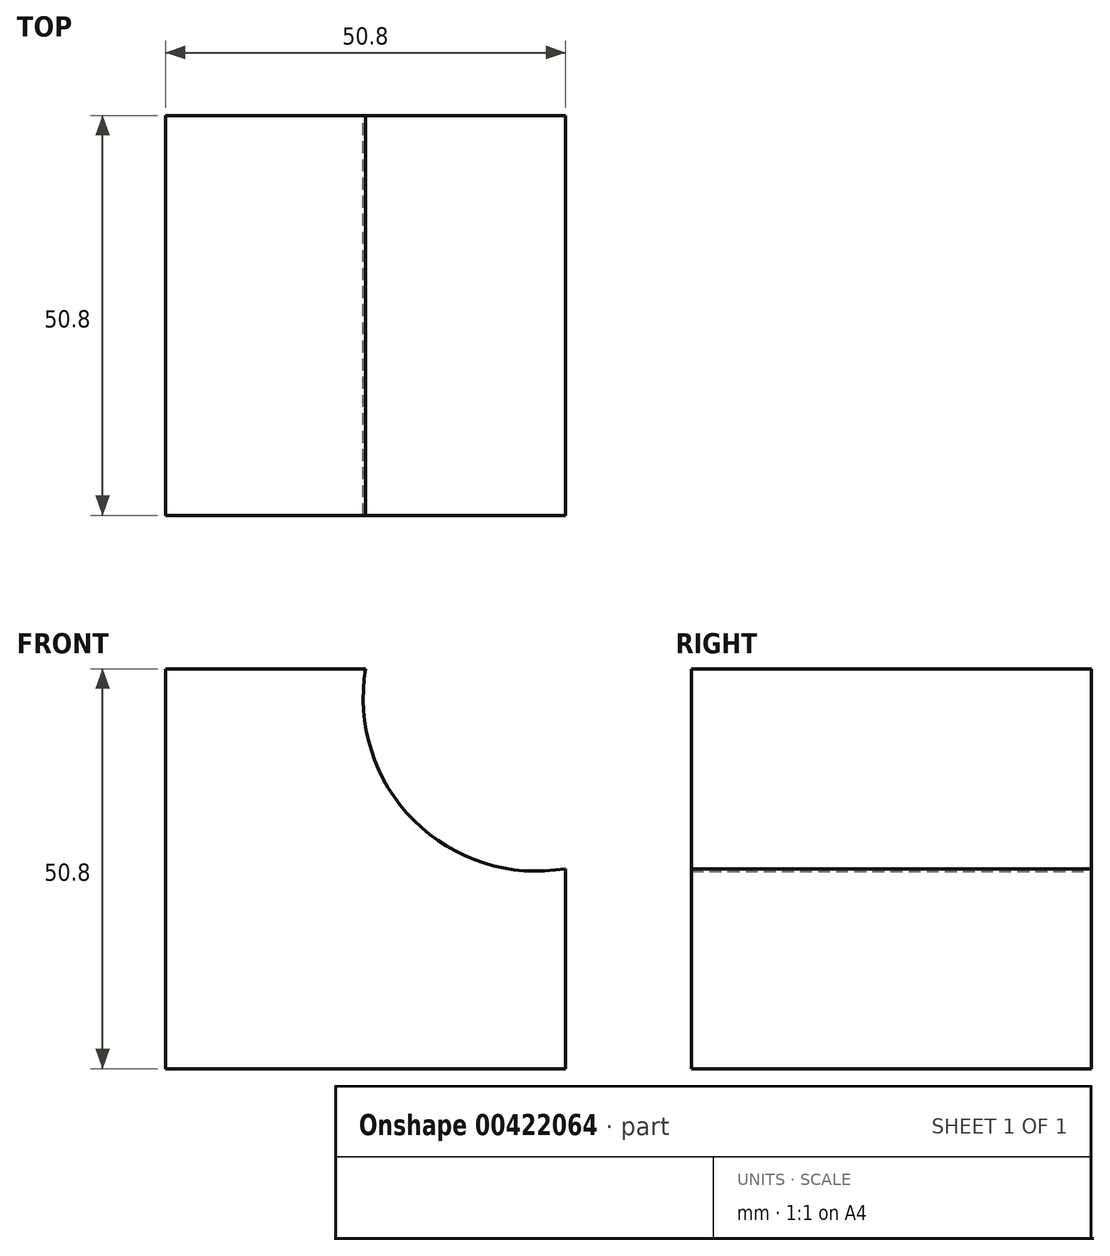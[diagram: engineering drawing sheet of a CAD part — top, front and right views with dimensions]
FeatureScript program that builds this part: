
annotation { "Feature Type Name" : "Feature", "Feature Type Description" : "" }
export const myFeature = defineFeature(function(context is Context, id is Id, definition is map)
    precondition{}
    {
        {
            var Q0;
            Q0=qCreatedBy(makeId("Front.planeOp"),FACE);
            var sketch = newSketch(context, id + "F0", { "sketchPlane" : qUnion([Q0])});
            skLineSegment(sketch, "E0", {"start": v(0, 0) * mm, "end": v(-50.8, 0) * mm});
            skLineSegment(sketch, "E1", {"start": v(-50.8, 0) * mm, "end": v(-50.8, 50.8) * mm});
            skLineSegment(sketch, "E2", {"start": v(-50.8, 50.8) * mm, "end": v(-25.4, 50.8) * mm});
            skLineSegment(sketch, "E3", {"start": v(0, 0) * mm, "end": v(0, 25.4) * mm});
            skArc(sketch, "E4", {"start": v(-25.4, 50.8) * mm, "mid": v(-19.26, 31.54) * mm, "end": v(0, 25.4) * mm});
            skSolve(sketch);
        }
        {
            var Q0;
            Q0=makeQuery(id+"F0.imprint","IMPRINT",FACE,{"disambiguationData":[TD([[makeQuery(id+"F0.imprint","IMPRINT",EDGE,{"derivedFrom":sQuery(id+"F0.wireOp",EDGE,"E0")}),-1.0]])]});
            extrude(context, id + "F1", {"entities" : qUnion([Q0]), "depth" : 50.8 * mm});
        }
    });
